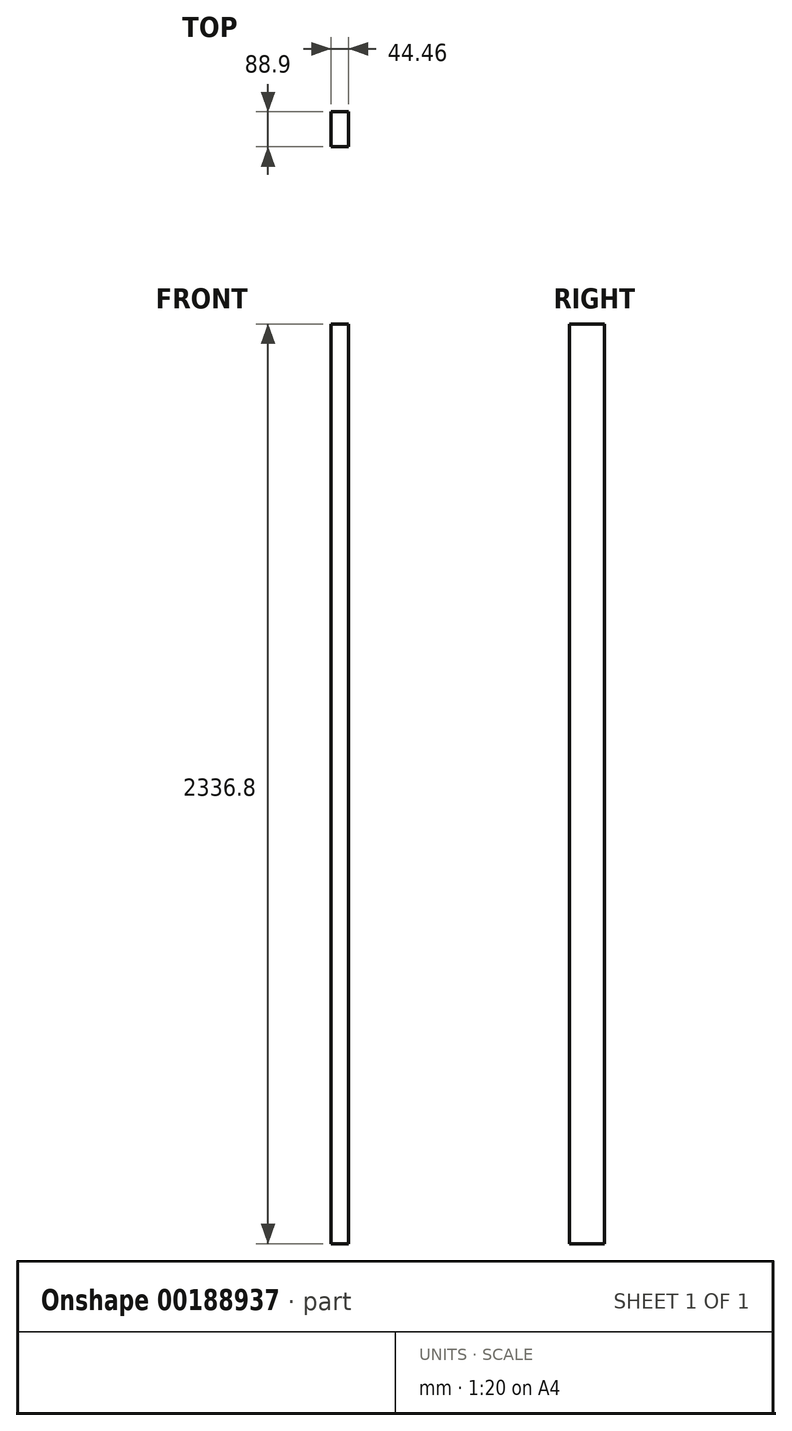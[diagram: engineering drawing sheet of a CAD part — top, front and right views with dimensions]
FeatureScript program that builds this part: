
annotation { "Feature Type Name" : "Feature", "Feature Type Description" : "" }
export const myFeature = defineFeature(function(context is Context, id is Id, definition is map)
    precondition{}
    {
        {
            var Q0;
            Q0=qCreatedBy(makeId("Top.planeOp"),FACE);
            var sketch = newSketch(context, id + "F1", { "sketchPlane" : qUnion([Q0])});
            skLineSegment(sketch, "E0.bottom", {"start": v(22.23, -44.45) * mm, "end": v(-22.22, -44.45) * mm});
            skLineSegment(sketch, "E0.top", {"start": v(22.22, 44.45) * mm, "end": v(-22.23, 44.45) * mm});
            skLineSegment(sketch, "E0.left", {"start": v(22.23, -44.45) * mm, "end": v(22.22, 44.45) * mm});
            skLineSegment(sketch, "E0.right", {"start": v(-22.22, -44.45) * mm, "end": v(-22.23, 44.45) * mm});
            skPoint(sketch, "E0.middle", {"position": v(0, 0) * mm});
            skSolve(sketch);
        }
        {
            var Q0;
            Q0=makeQuery(id+"F1.imprint","IMPRINT",FACE,{"disambiguationData":[TD([[makeQuery(id+"F1.imprint","IMPRINT",EDGE,{"derivedFrom":sQuery(id+"F1.wireOp",EDGE,"E0.bottom")}),-1.0]])]});
            extrude(context, id + "F0", {"entities" : qUnion([Q0]), "endBound" : BoundingType.SYMMETRIC, "depth" : 2336.8 * mm});
        }
    });
